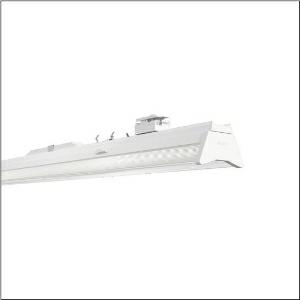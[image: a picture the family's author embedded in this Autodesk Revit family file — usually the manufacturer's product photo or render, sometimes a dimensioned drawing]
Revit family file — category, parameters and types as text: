
# Revit family: licross_r__21_performance_mo_52td16cn49xg_b518
name_source: partatom
category: Lighting Fixtures
units: mm (PartAtom-declared; Revit-internal decimal feet)

## family parameters
Cut with Voids When Loaded = No
Host = Face
Light Source = No
Part Type = Normal
Room Calculation Point = No
Round Connector Dimension = Use Diameter
Shared = No

## types (1)
- --- (1 x LED, 9240 lm, 50.4 W, 4000K)
    Apparent Load = 50 VA
    CIE Flux Codes = 66 88 96 79 100
    Color Rendering = 80
    Color Temperature = 4000K
    Default Elevation = 1800 mm
    Description = Licross® 21 Performance MO, luminaire insert, of sheet steel, galvanised, coil coated, white, length: 1.500mm, width: 120mm, height: 123mm, LED rated luminous flux: 9.240lm, light colour: 840, control gear: ON/OFF Multilumen, CLOi, control gear: ECG Multilumen, with plug, 3-pole, with phase selection, mains connection: 220..240V, AC, 50/60Hz, start of lifetime: 50W, end of service life: 61W, internal wiring halogen-free, primary light control with lens, of plastic, primary optical cover: cover, of PMMA, light emission: direct/indirect distribution, primary light characteristic: symmetric, protection rating (complete): IP54, insulation class (complete): insulation class I (protective earthing), certification: CE, ENEC, UKCA, protection symbol: D if used in an environment with non-conductive dust loads with corresponding accessories, impact resistance: IK06, permissible ambient temperature for indoor applications: -35..+45°C, corresponds to IFS (International Featured Standards) requirements for safety and quality in the food industry, reducing of maximum allowable ambient temperature of 5°C with ceiling mounting, LABS conformity tested according to VDMA 24364:2018-05, packaging unit: 1 piece
    Height = 114 mm
    Lamp = 1 x LED
    Lamp Light Flux = 9240 lm
    Lamp Power = 50.4 W
    Lamp count = 1
    Length = 1500 mm
    Luminous efficacy = 183 lm/W
    Manufacturer = Siteco
    ModVariant = No
    Model = 52TD16CN49XG
    Mounting Place = Ceiling
    Mounting Type = Pendant
    Number of Poles = 1
    OnlyDefault = Yes
    Power Factor = 1
    Product Name = Licross® 21 Performance MO
    Product group = luminaire insert | ceiling pendant
    ProductGroupID = 902
    Protection Class = Protection class I
    Protection Degree = IP 54
    RLX_Detail_Level = 1
    RLX_Emergency_Light_Flux = 0 lm
    RLX_Emergency_Type = 0
    RLX_Emergency_Type_DB = No
    RlxData = <blob elided: 31953 chars, md5=17c9b07d>
    Socket = socket
    Standby Power = 0 W
    System Light Flux = 9240 lm
    System Power = 50 W
    Type Comments = factory setting: luminous flux: 100 % | (A | C | E) | 117 mA
    Type Image = l_1256138.jpg
    URL = http://relux.com
    VarID = @adj_133043
    Voltage = 0 V
    Weight = 0.00 kg
    Width = 120 mm

## geometry (parser evidence)
native form markers: Blend x4, Sweep x12
no freeform markers — native parametric forms only
